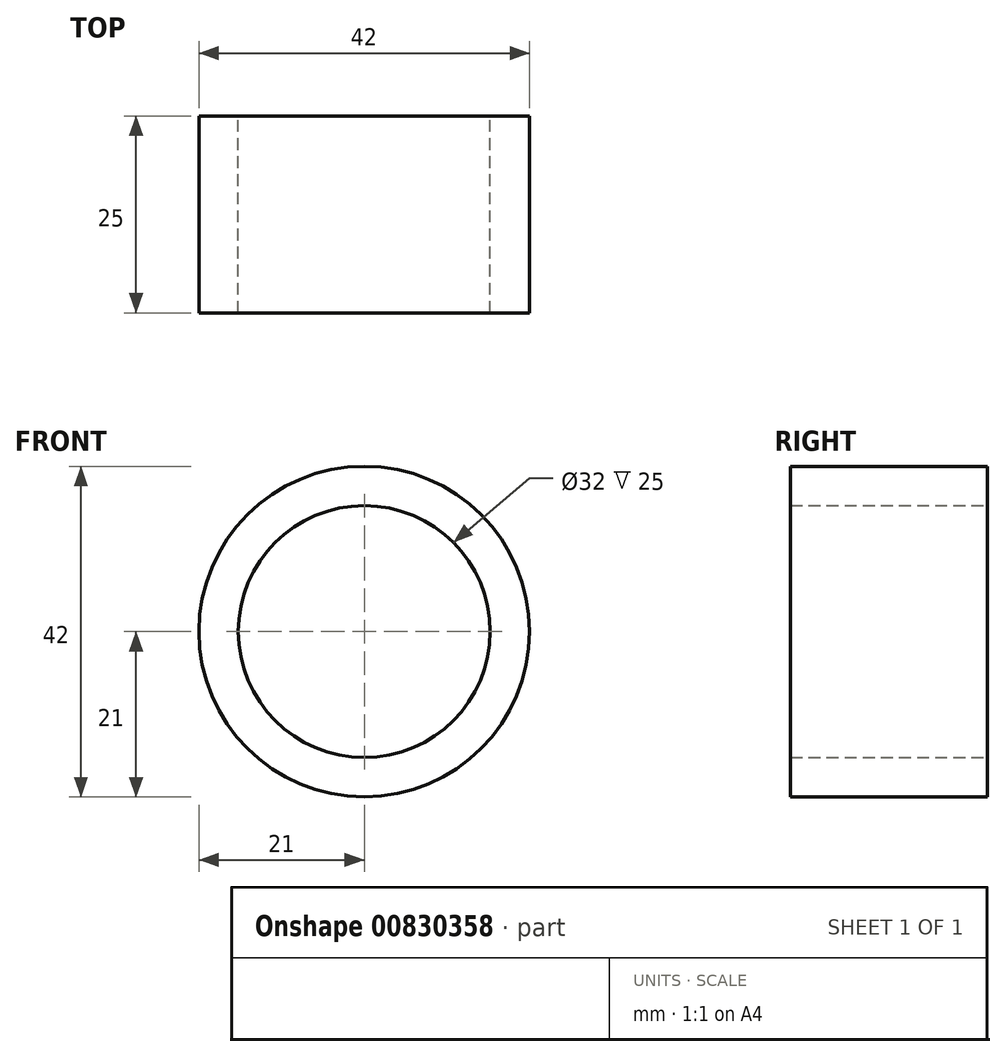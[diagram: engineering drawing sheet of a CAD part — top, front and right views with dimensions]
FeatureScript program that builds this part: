
annotation { "Feature Type Name" : "Feature", "Feature Type Description" : "" }
export const myFeature = defineFeature(function(context is Context, id is Id, definition is map)
    precondition{}
    {
        {
            var Q0;
            Q0=qCreatedBy(makeId("Front.planeOp"),FACE);
            var sketch = newSketch(context, id + "F0", { "sketchPlane" : qUnion([Q0])});
            skCircle(sketch, "E0", {"center": v(0, 0) * mm, "radius": 16 * mm});
            skCircle(sketch, "E1.0", {"center": v(0, 0) * mm, "radius": 21 * mm});
            skSolve(sketch);
        }
        {
            var Q0;
            Q0 = qSketchRegion(id + "F0", true);
            extrude(context, id + "F1", {"entities" : qUnion([Q0]), "depth" : 25 * mm, "offsetDistance" : 25 * mm});
        }
        {
            var Q0;
            Q0=qCreatedBy(makeId("Right.planeOp"),FACE);
            cPlane(context, id + "F2", {"entities" : qUnion([Q0]), "cplaneType" : CPlaneType.OFFSET, "offset" : 21 * mm, "width" : 150 * mm, "height" : 150 * mm});
        }
    });
